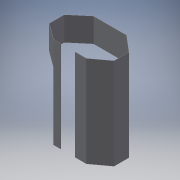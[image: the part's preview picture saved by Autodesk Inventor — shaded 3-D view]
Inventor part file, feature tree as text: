
AUTODESK INVENTOR PART (.ipt)
format: ipt  version: 2016 (Build 200138000, 138)  size: 251,392 bytes
history: native  units: mm
features: sketch x11, extrude x11, plane x1, shell x1
ambient origin geometry x8: Origin, YZ Plane, XZ Plane, XY Plane, X Axis, Y Axis, Z Axis, Center Point
bodies: Body1 (feature_tree)
feature tree (24):
  sketch  "Sketch2"  dims[d19=673.0mm d20=275.5mm d21=251.0mm]
  plane  "Work Plane1"
  extrude  "Extrusion1"  Depth=275.5mm
  shell  "Shell2"  Thickness=251.0mm
  extrude  "Extrusion2"  Depth=331.0mm
  extrude  "Extrusion3"  Depth=534.0mm
  extrude  "Extrusion4"  Depth=3.0mm
  extrude  "Extrusion5"  Depth=3.0mm TaperAngle=0.0deg
  extrude  "Extrusion6"  TaperAngle=180.0deg  [1 undecoded]
  extrude  "Extrusion7"  Depth=122.0mm
  extrude  "Extrusion8"  Depth=190.0mm
  extrude  "Extrusion9"  Depth=3.0mm TaperAngle=0.0deg
  extrude  "Extrusion10"  Depth=225.0mm TaperAngle=0.0deg
  extrude  "Extrusion11"  Depth=10.0mm TaperAngle=0.0deg
  sketch  "Sketch4"  dims[d22=349.0mm d23=331.0mm]
  sketch  "Sketch5"  dims[d24=275.5mm d25=534.0mm]
  sketch  "Sketch6"  dims[d26=200.0mm d44=1306.0mm d45=0.0mm d46=3.0mm]
  sketch  "Sketch7"  dims[d47=3.0mm d48=0.0mm d49=3.0mm d50=0.0mm]
  sketch  "Sketch8"  dims[d51=400.0mm d52=180.0deg]
  sketch  "Sketch9"  dims[d53=816.377mm d54=0.0mm d55=122.0mm]
  sketch  "Sketch10"  dims[d56=900.0mm d57=0.0mm d58=190.0mm]
  sketch  "Sketch11"  dims[d59=900.0mm d60=0.0mm d61=3.0mm d62=0.0mm]
  sketch  "Sketch12"  dims[d63=225.0mm d64=0.0mm d65=225.0mm d66=0.0mm]
  sketch  "Sketch15"  dims[d67=1.321mm d68=3.0mm d69=0.0mm d95=23.0mm d97=167.0mm d98=10.0mm d99=10.0mm d100=20.0mm d101=20.0mm d102=3.0mm d103=0.0mm]
note: 1 required parameter value undecoded (feature->parameter linkage not recoverable at this tier; creation-order binding heuristic only, values carry confidence <= 0.55)
